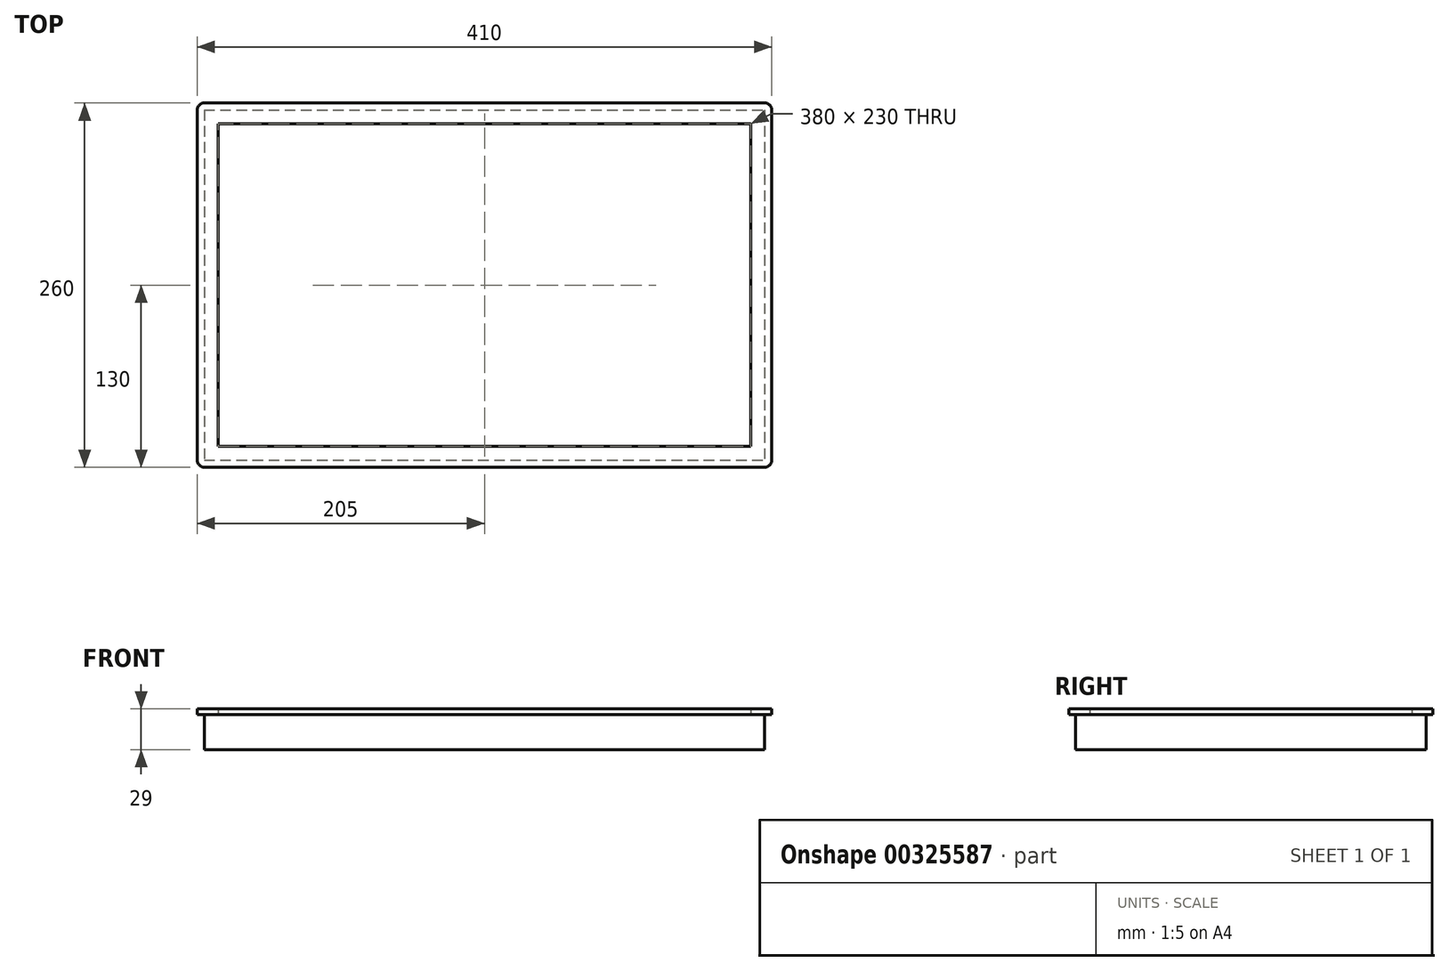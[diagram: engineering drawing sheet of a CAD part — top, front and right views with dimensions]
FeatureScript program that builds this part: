
annotation { "Feature Type Name" : "Feature", "Feature Type Description" : "" }
export const myFeature = defineFeature(function(context is Context, id is Id, definition is map)
    precondition{}
    {
        {
            var Q0;
            Q0=qCreatedBy(makeId("Top.planeOp"),FACE);
            var sketch = newSketch(context, id + "F0", { "sketchPlane" : qUnion([Q0])});
            skLineSegment(sketch, "E0.bottom", {"start": v(-200, 125) * mm, "end": v(200, 125) * mm});
            skLineSegment(sketch, "E0.top", {"start": v(-200, -125) * mm, "end": v(200, -125) * mm});
            skLineSegment(sketch, "E0.left", {"start": v(-200, 125) * mm, "end": v(-200, -125) * mm});
            skLineSegment(sketch, "E0.right", {"start": v(200, 125) * mm, "end": v(200, -125) * mm});
            skPoint(sketch, "E0.middle", {"position": v(0, 0) * mm});
            skSolve(sketch);
        }
        {
            var Q0;
            Q0=makeQuery(id+"F0.imprint","IMPRINT",FACE,{"disambiguationData":[TD([[makeQuery(id+"F0.imprint","IMPRINT",EDGE,{"derivedFrom":sQuery(id+"F0.wireOp",EDGE,"E0.bottom")}),-1.0]])]});
            extrude(context, id + "F1", {"entities" : qUnion([Q0]), "depth" : 25 * mm});
        }
        {
            var Q0;
            Q0=makeQuery(id+"F1.opExtrude","CAP_FACE",FACE,{"disambiguationData":[OSD([sQuery(id+"F0.wireOp",EDGE,"E0.bottom"),sQuery(id+"F0.wireOp",EDGE,"E0.top"),sQuery(id+"F0.wireOp",EDGE,"E0.left"),sQuery(id+"F0.wireOp",EDGE,"E0.right")])],"isStart":false});
            var sketch = newSketch(context, id + "F2", { "sketchPlane" : qUnion([Q0])});
            skLineSegment(sketch, "E1.bottom", {"start": v(-190, 115) * mm, "end": v(190, 115) * mm});
            skLineSegment(sketch, "E1.top", {"start": v(-190, -115) * mm, "end": v(190, -115) * mm});
            skLineSegment(sketch, "E1.left", {"start": v(-190, 115) * mm, "end": v(-190, -115) * mm});
            skLineSegment(sketch, "E1.right", {"start": v(190, 115) * mm, "end": v(190, -115) * mm});
            skPoint(sketch, "E1.middle", {"position": v(0, 0) * mm});
            skLineSegment(sketch, "E2.bottom", {"start": v(-205, 130) * mm, "end": v(205, 130) * mm});
            skLineSegment(sketch, "E2.top", {"start": v(-205, -130) * mm, "end": v(205, -130) * mm});
            skLineSegment(sketch, "E2.left", {"start": v(-205, 130) * mm, "end": v(-205, -130) * mm});
            skLineSegment(sketch, "E2.right", {"start": v(205, 130) * mm, "end": v(205, -130) * mm});
            skSolve(sketch);
        }
        {
            var Q0;
            Q0 = qSketchRegion(id + "F2", true);
            extrude(context, id + "F3", {"entities" : qUnion([Q0]), "depth" : 4 * mm});
        }
        {
            var Q0;
            Q0=makeQuery(id+"F3.opExtrude","SWEPT_EDGE",EDGE,{"disambiguationData":[OSD([sQuery(id+"F2.wireOp",EDGE,"E2.top"),sQuery(id+"F2.wireOp",EDGE,"E2.left")])]});
            var Q1;
            Q1=makeQuery(id+"F3.opExtrude","SWEPT_EDGE",EDGE,{"disambiguationData":[OSD([sQuery(id+"F2.wireOp",EDGE,"E2.bottom"),sQuery(id+"F2.wireOp",EDGE,"E2.left")])]});
            var Q2;
            Q2=makeQuery(id+"F3.opExtrude","SWEPT_EDGE",EDGE,{"disambiguationData":[OSD([sQuery(id+"F2.wireOp",EDGE,"E2.top"),sQuery(id+"F2.wireOp",EDGE,"E2.right")])]});
            var Q3;
            Q3=makeQuery(id+"F3.opExtrude","SWEPT_EDGE",EDGE,{"disambiguationData":[OSD([sQuery(id+"F2.wireOp",EDGE,"E2.bottom"),sQuery(id+"F2.wireOp",EDGE,"E2.right")])]});
            fillet(context, id + "F4", {"entities" : qUnion([Q0, Q1, Q2, Q3]), "radius" : 5 * mm, "tangentPropagation" : true, "allowEdgeOverflow" : false});
        }
    });
